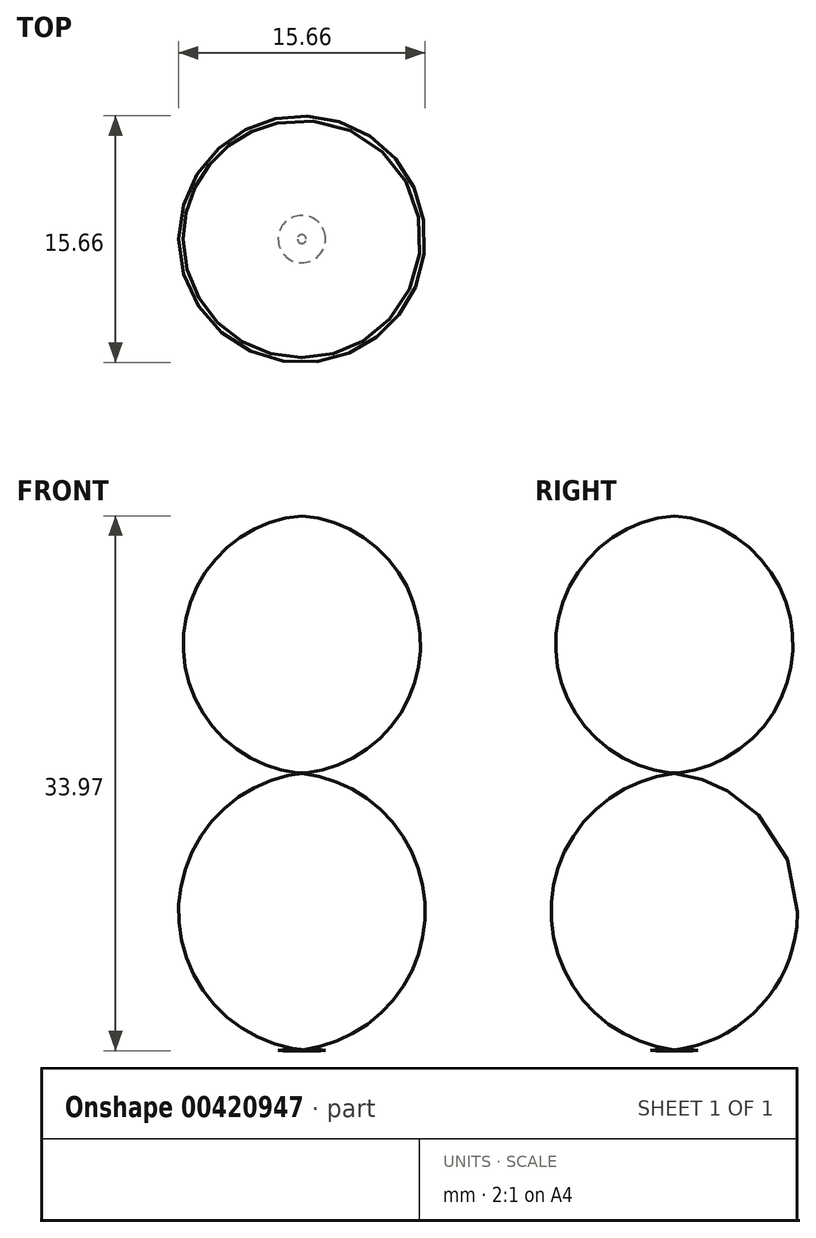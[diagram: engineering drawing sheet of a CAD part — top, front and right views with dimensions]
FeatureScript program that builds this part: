
annotation { "Feature Type Name" : "Feature", "Feature Type Description" : "" }
export const myFeature = defineFeature(function(context is Context, id is Id, definition is map)
    precondition{}
    {
        {
            var Q0;
            Q0=qCreatedBy(makeId("Front.planeOp"),FACE);
            var sketch = newSketch(context, id + "F0", { "sketchPlane" : qUnion([Q0])});
            skLineSegment(sketch, "E0", {"start": v(0, 52.28) * mm, "end": v(0, -62.7) * mm});
            skArc(sketch, "E1", {"start": v(0, 19.57) * mm, "mid": v(15.07, 35.93) * mm, "end": v(0, 52.28) * mm});
            skArc(sketch, "E2", {"start": v(0, -15.54) * mm, "mid": v(19.69, 2.01) * mm, "end": v(0, 19.57) * mm});
            skArc(sketch, "E3", {"start": v(0, -62.7) * mm, "mid": v(24.41, -39.12) * mm, "end": v(0, -15.54) * mm});
            skSolve(sketch);
        }
        {
            var Q0;
            Q0 = qSketchRegion(id + "F0", true);
            var Q1;
            Q1=sQuery(id+"F0.wireOp",EDGE,"E0");
            revolve(context, id + "F1", {"entities" : qUnion([Q0]), "axis" : qUnion([Q1]), "revolveType" : RevolveType.FULL});
        }
        {
            var Q0;
            Q0=makeQuery(id+"F1.opRevolve","SWEPT_BODY",BODY,{"disambiguationData":[OSD([sQuery(id+"F0.wireOp",EDGE,"E0"),sQuery(id+"F0.wireOp",EDGE,"E1"),sQuery(id+"F0.wireOp",EDGE,"E2"),sQuery(id+"F0.wireOp",EDGE,"E3")])]});
            var Q1;
            Q1=qCreatedBy(makeId("Origin.pointOp"),VERTEX);
            var Q2;
            Q2=qCreatedBy(makeId("Origin.pointOp"),VERTEX);
            transform(context, id + "F2", {"entities" : qUnion([Q0]), "transformType" : TransformType.SCALE_UNIFORMLY, "scale" : 2 / 4, "scalePoint" : qUnion([Q2]), "makeCopy" : false});
        }
    });
